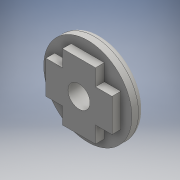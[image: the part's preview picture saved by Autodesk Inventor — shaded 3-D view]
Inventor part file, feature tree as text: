
AUTODESK INVENTOR PART (.ipt)
format: ipt  version: 2016 (Build 200138000, 138)  size: 147,456 bytes
history: native  units: mm
features: other x4, extrude x2, hole x2, fillet x1
ambient origin geometry x8: Origin, YZ Plane, XZ Plane, XY Plane, X Axis, Y Axis, Z Axis, Center Point
bodies: Body1 (feature_tree)
feature tree (9):
  other  "zero_sketch.ipt"
  extrude  "Extrusion1"  Depth=10.0mm
  extrude  "Extrusion2"  Depth=0.6mm TaperAngle=0.0deg
  hole  "Hole1"  [1 undecoded]
  hole  "Hole2"  [1 undecoded]
  fillet  "Fillet1"  Radius=10.0mm
  other  "base+body"
  other  "base+body_1"
  other  "base+body_2"
note: 2 required parameter values undecoded (feature->parameter linkage not recoverable at this tier; creation-order binding heuristic only, values carry confidence <= 0.55)
